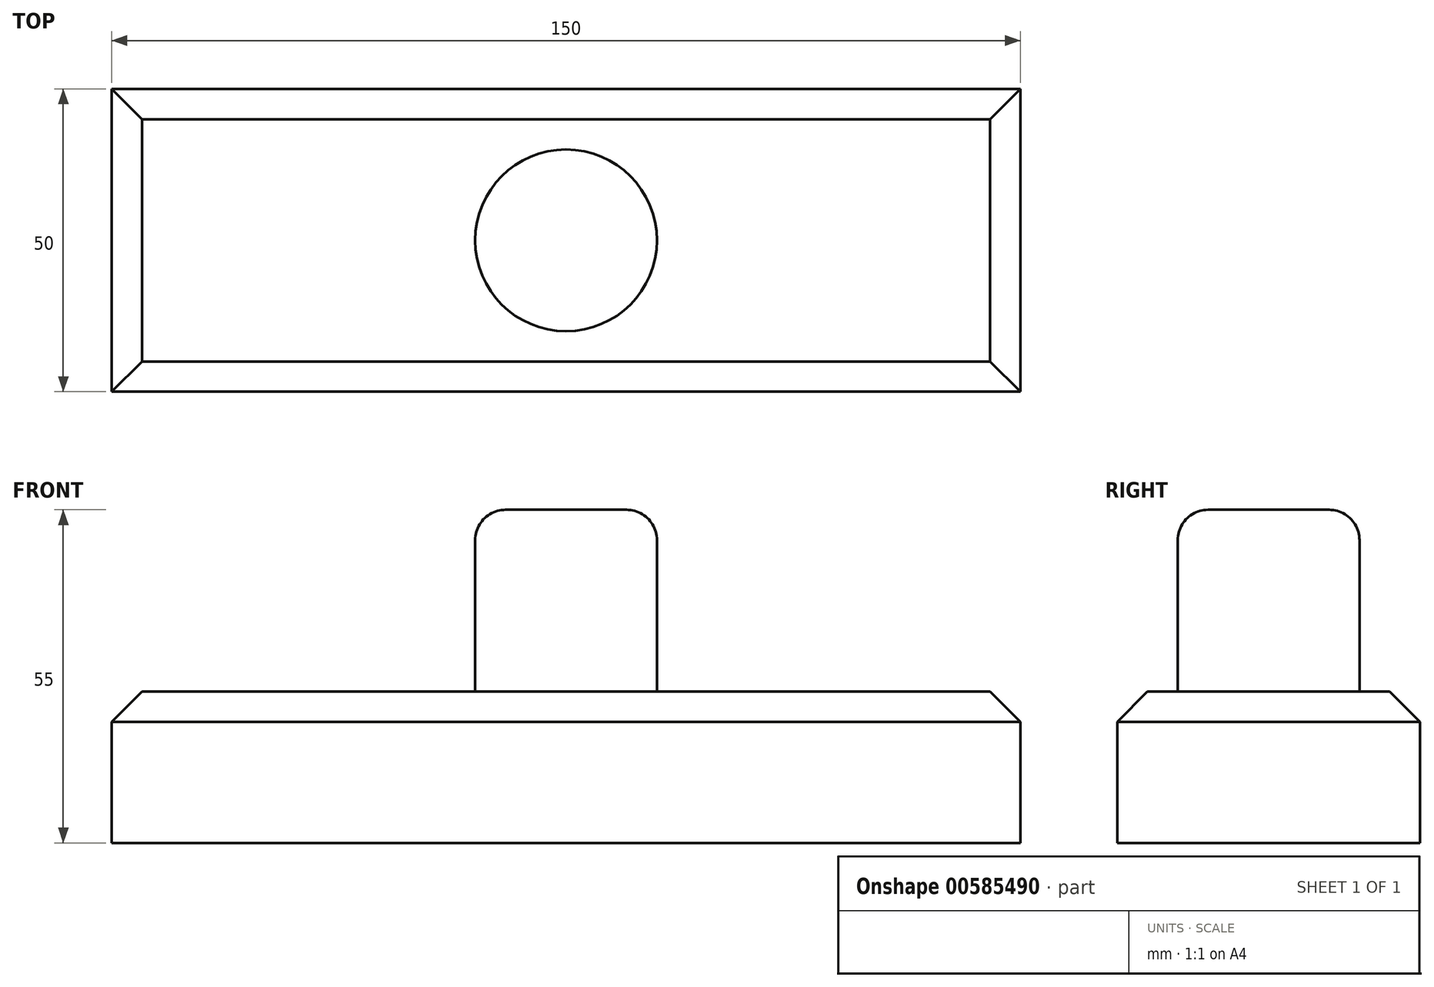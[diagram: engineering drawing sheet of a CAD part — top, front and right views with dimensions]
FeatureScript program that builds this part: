
annotation { "Feature Type Name" : "Feature", "Feature Type Description" : "" }
export const myFeature = defineFeature(function(context is Context, id is Id, definition is map)
    precondition{}
    {
        {
            var Q0;
            Q0=qCreatedBy(makeId("Top.planeOp"),FACE);
            var sketch = newSketch(context, id + "F0", { "sketchPlane" : qUnion([Q0])});
            skLineSegment(sketch, "E0.bottom", {"start": v(-61.43, 12.63) * mm, "end": v(88.57, 12.63) * mm});
            skLineSegment(sketch, "E0.top", {"start": v(-61.43, -37.37) * mm, "end": v(88.57, -37.37) * mm});
            skLineSegment(sketch, "E0.left", {"start": v(-61.43, 12.63) * mm, "end": v(-61.43, -37.37) * mm});
            skLineSegment(sketch, "E0.right", {"start": v(88.57, 12.63) * mm, "end": v(88.57, -37.37) * mm});
            skSolve(sketch);
        }
        {
            var Q0;
            Q0=makeQuery(id+"F0.imprint","IMPRINT",FACE,{"disambiguationData":[TD([[makeQuery(id+"F0.imprint","IMPRINT",EDGE,{"derivedFrom":sQuery(id+"F0.wireOp",EDGE,"E0.bottom")}),-1.0]])]});
            extrude(context, id + "F1", {"entities" : qUnion([Q0]), "depth" : 25 * mm, "offsetDistance" : 25 * mm});
        }
        {
            var Q0;
            Q0=makeQuery(id+"F1.opExtrude","CAP_FACE",FACE,{"disambiguationData":[OSD([sQuery(id+"F0.wireOp",EDGE,"E0.bottom"),sQuery(id+"F0.wireOp",EDGE,"E0.top"),sQuery(id+"F0.wireOp",EDGE,"E0.left"),sQuery(id+"F0.wireOp",EDGE,"E0.right")])],"isStart":false});
            var sketch = newSketch(context, id + "F2", { "sketchPlane" : qUnion([Q0])});
            skCircle(sketch, "E1", {"center": v(13.57, -12.37) * mm, "radius": 15 * mm});
            skPoint(sketch, "E1.first.point", {"position": v(-1.3, -14.4) * mm});
            skPoint(sketch, "E1.second.point", {"position": v(22.06, 0) * mm});
            skPoint(sketch, "E1.third.point", {"position": v(24.47, -22.68) * mm});
            skLineSegment(sketch, "E2", {"start": v(-61.43, -12.37) * mm, "end": v(88.57, -12.37) * mm});
            skSolve(sketch);
        }
        {
            var Q0;
            Q0 = qSketchRegion(id + "F2", true);
            extrude(context, id + "F3", {"entities" : qUnion([Q0]), "operationType" : NewBodyOperationType.ADD, "depth" : 30 * mm, "offsetDistance" : 25 * mm});
        }
        {
            var Q0;
            Q0=makeQuery(id+"F3.opExtrude","CAP_EDGE",EDGE,{"disambiguationData":[OSD([sQuery(id+"F2.wireOp",EDGE,"E1")])],"isStart":false});
            fillet(context, id + "F4", {"entities" : qUnion([Q0]), "radius" : 5 * mm, "tangentPropagation" : true, "allowEdgeOverflow" : false});
        }
        {
            var Q0;
            Q0=makeQuery(id+"F1.opExtrude","CAP_EDGE",EDGE,{"disambiguationData":[OSD([sQuery(id+"F0.wireOp",EDGE,"E0.left")])],"isStart":false});
            var Q1;
            Q1=makeQuery(id+"F1.opExtrude","CAP_EDGE",EDGE,{"disambiguationData":[OSD([sQuery(id+"F0.wireOp",EDGE,"E0.top")])],"isStart":false});
            var Q2;
            Q2=makeQuery(id+"F1.opExtrude","CAP_EDGE",EDGE,{"disambiguationData":[OSD([sQuery(id+"F0.wireOp",EDGE,"E0.bottom")])],"isStart":false});
            var Q3;
            Q3=makeQuery(id+"F1.opExtrude","CAP_EDGE",EDGE,{"disambiguationData":[OSD([sQuery(id+"F0.wireOp",EDGE,"E0.right")])],"isStart":false});
            chamfer(context, id + "F5", {"entities" : qUnion([Q0, Q1, Q2, Q3]), "width" : 5 * mm, "tangentPropagation" : true});
        }
    });
